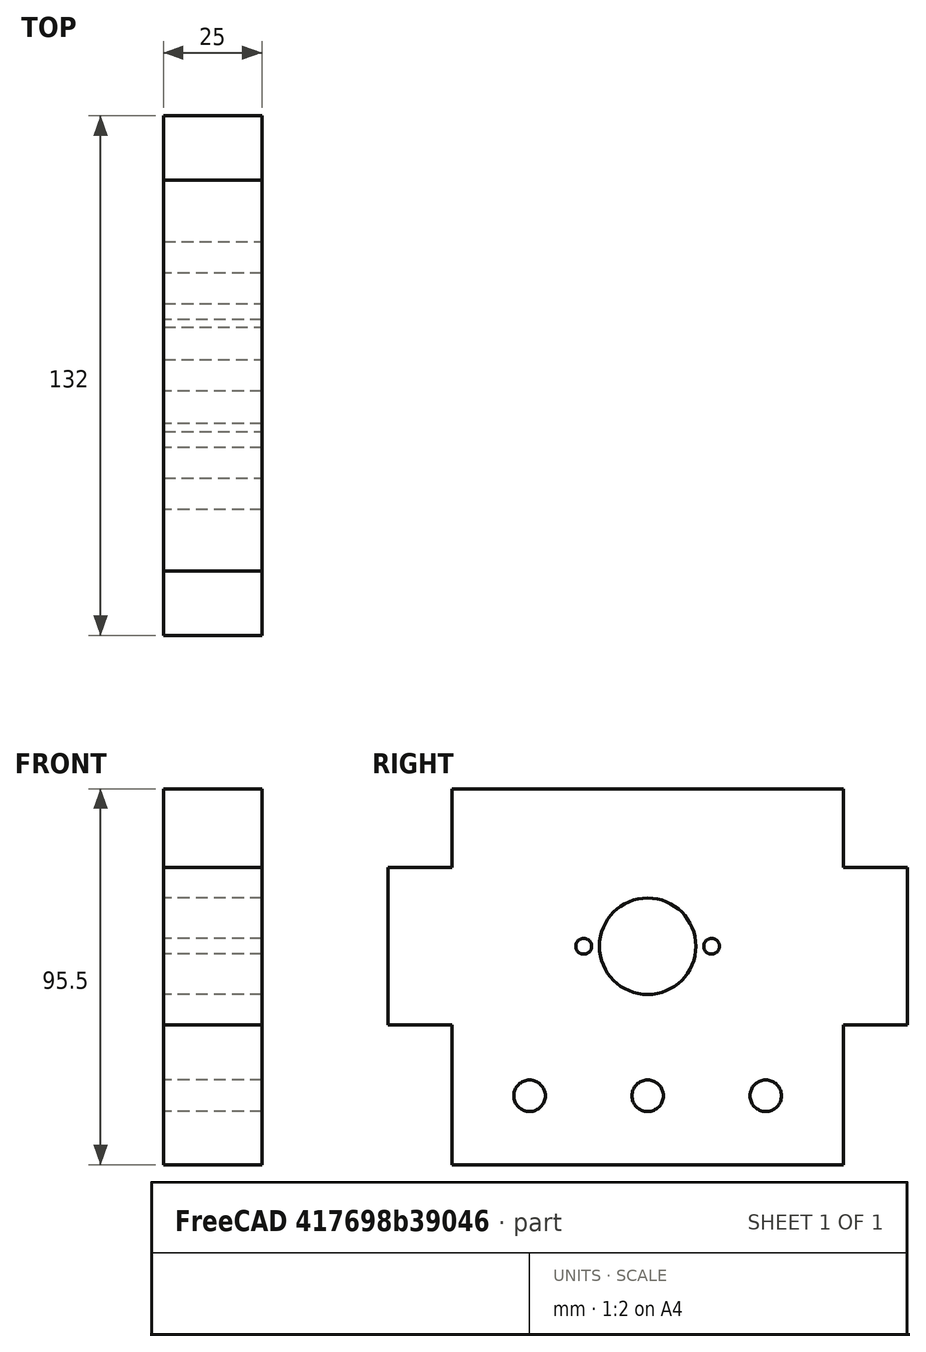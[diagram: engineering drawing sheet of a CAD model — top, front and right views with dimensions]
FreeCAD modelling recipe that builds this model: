
FCSTD DOCUMENT  (FreeCAD 0.19R24267 +99 (Git))
Label: V2 Tabbed end plate FEA_CLEARED
License: All rights reserved
LicenseURL: http://en.wikipedia.org/wiki/All_rights_reserved
objects: Sketcher::SketchObject×4, PartDesign::Pad×4, Fem::ConstraintForce×2, Fem::FeaturePython×2, PartDesign::Body×1, Fem::FemSolverObjectPython×1, App::MaterialObjectPython×1, Fem::ConstraintFixed×1, Fem::FemMeshObjectPython×1, Fem::FemAnalysis×1
note: 13 computed .brp shape members not serialized (recipe doc carries the construction recipe); baked Part::Feature solids carry a one-line shape summary decoded from their .brp

FEATURE [Sketcher::SketchObject] Sketch
  FullyConstrained = true
  MapMode = 5
  Placement = pos=(0,0,0) rot=(0.57735,0.57735,0.57735;2.0944rad)
  Support = -> [YZ_Plane]
  sketch-geometry (41):
    g0: LineSegment StartX=-49.7 StartY=40 StartZ=0 EndX=49.7 EndY=40 EndZ=0
    g1: LineSegment StartX=49.7 StartY=40 StartZ=0 EndX=49.7 EndY=20 EndZ=0
    g2: LineSegment StartX=49.7 StartY=-55.5 StartZ=0 EndX=-49.7 EndY=-55.5 EndZ=0
    g3: LineSegment StartX=-49.7 StartY=-55.5 StartZ=0 EndX=-49.7 EndY=-20 EndZ=0
    g4: Circle CenterX=0 CenterY=0 CenterZ=0 NormalX=0 NormalY=0 NormalZ=1 AngleXU=0 Radius=12.25
    g5: LineSegment StartX=-49.7 StartY=20 StartZ=0 EndX=-66 EndY=20 EndZ=0
    g6: LineSegment StartX=-66 StartY=20 StartZ=0 EndX=-66 EndY=-20 EndZ=0
    g7: LineSegment StartX=-66 StartY=-20 StartZ=0 EndX=-49.7 EndY=-20 EndZ=0
    g8: LineSegment StartX=49.7 StartY=20 StartZ=0 EndX=66 EndY=20 EndZ=0
    g9: LineSegment StartX=49.7 StartY=-20 StartZ=0 EndX=66 EndY=-20 EndZ=0
    g10: LineSegment StartX=66 StartY=20 StartZ=0 EndX=66 EndY=-20 EndZ=0
    g11: LineSegment StartX=-49.7 StartY=20 StartZ=0 EndX=-49.7 EndY=40 EndZ=0
    g12: LineSegment StartX=49.7 StartY=-20 StartZ=0 EndX=49.7 EndY=-55.5 EndZ=0
    g13: Circle CenterX=-16.25 CenterY=0 CenterZ=0 NormalX=0 NormalY=0 NormalZ=1 AngleXU=0 Radius=2
    g14: Circle CenterX=16.25 CenterY=0 CenterZ=0 NormalX=0 NormalY=0 NormalZ=1 AngleXU=0 Radius=2
    g15: Circle CenterX=0 CenterY=0 CenterZ=0 NormalX=0 NormalY=0 NormalZ=1 AngleXU=0 Radius=20.25
    g16: Circle CenterX=-16.25 CenterY=0 CenterZ=0 NormalX=0 NormalY=0 NormalZ=1 AngleXU=0 Radius=4
    g17: Circle CenterX=16.25 CenterY=0 CenterZ=0 NormalX=0 NormalY=0 NormalZ=1 AngleXU=0 Radius=4
    g18: LineSegment StartX=-16.25 StartY=2 StartZ=0 EndX=-16.25 EndY=-2 EndZ=0
    g19: LineSegment StartX=-18.25 StartY=0 StartZ=0 EndX=-14.25 EndY=0 EndZ=0
    g20: LineSegment StartX=14.25 StartY=0 StartZ=0 EndX=18.25 EndY=0 EndZ=0
    g21: LineSegment StartX=16.25 StartY=2 StartZ=0 EndX=16.25 EndY=-2 EndZ=0
    g22: Circle CenterX=0 CenterY=-38 CenterZ=0 NormalX=0 NormalY=0 NormalZ=1 AngleXU=0 Radius=4
    g23: LineSegment StartX=-30 StartY=-38 StartZ=0 EndX=30 EndY=-38 EndZ=0
    g24: Circle CenterX=-30 CenterY=-38 CenterZ=0 NormalX=0 NormalY=0 NormalZ=1 AngleXU=0 Radius=4
    g25: Circle CenterX=30 CenterY=-38 CenterZ=0 NormalX=0 NormalY=0 NormalZ=1 AngleXU=0 Radius=4
    g26: GeomPoint X=0 Y=-55.5 Z=0
    g27: Circle CenterX=0 CenterY=0 CenterZ=0 NormalX=0 NormalY=0 NormalZ=1 AngleXU=0 Radius=13.4
    g28: Circle CenterX=0 CenterY=-42.25 CenterZ=0 NormalX=0 NormalY=0 NormalZ=1 AngleXU=0 Radius=8.25
    g29: GeomPoint X=0 Y=-34 Z=0
    g30: GeomPoint X=0 Y=-42 Z=0
    g31: GeomPoint X=0 Y=-50.5 Z=0
    g32: GeomPoint X=0 Y=35.75 Z=0
    g33: GeomPoint X=0 Y=31.5 Z=0
    g34: GeomPoint X=0 Y=40 Z=0
    g35: LineSegment StartX=-30 StartY=-34 StartZ=0 EndX=-30 EndY=-42 EndZ=0
    g36: LineSegment StartX=-34 StartY=-38 StartZ=0 EndX=-26 EndY=-38 EndZ=0
    g37: LineSegment StartX=-4 StartY=-38 StartZ=0 EndX=4 EndY=-38 EndZ=0
    g38: LineSegment StartX=0 StartY=-42 StartZ=0 EndX=0 EndY=-34 EndZ=0
    g39: LineSegment StartX=30 StartY=-34 StartZ=0 EndX=30 EndY=-42 EndZ=0
    g40: LineSegment StartX=26 StartY=-38 StartZ=0 EndX=34 EndY=-38 EndZ=0
  constraints (116):
    c: Coincident(g0,g1)
    c: Coincident(g12,g2)
    c: Coincident(g2,g3)
    c: Coincident(g11,g0)
    c: Horizontal(g2)
    c: Vertical(g3)
    c: Coincident(g4,g-1)
    c: DistanceX(g0,g0) = 99.4
    c: Symmetric(g0,g0,g-2)
    c: DistanceY(g4,g0) = 40
    c: Horizontal(g5)
    c: Coincident(g6,g5)
    c: Coincident(g7,g6)
    c: Horizontal(g7)
    c: Symmetric(g5,g6,g-1)
    c: Horizontal(g8)
    c: Coincident(g10,g8)
    c: Coincident(g10,g9)
    c: Symmetric(g5,g8,g-2)
    c: Symmetric(g6,g9,g-2)
    c: Horizontal(g9)
    c: DistanceY(g6,g6) = 40
    c: Coincident(g3,g7)
    c: Coincident(g11,g5)
    c: Tangent(g3,g11)
    c: Coincident(g1,g8)
    c: Coincident(g12,g9)
    c: Tangent(g1,g12)
    c: DistanceX(g6,g9) = 132
    c: PointOnObject(g13,g-1)
    c: Symmetric(g14,g13,g-2)
    c: Equal(g13,g14)
    c: Coincident(g15,g4)
    c: Coincident(g16,g13)
    c: Coincident(g17,g14)
    c: DistanceX(g13,g14) = 32.5
    c: Equal(g17,g16)
    c: Diameter(g4) = 24.5
    c: Diameter(g15) = 40.5
    c: Diameter(g13) = 4
    c: PointOnObject(g18,g13)
    c: PointOnObject(g18,g13)
    c: PointOnObject(g19,g13)
    c: PointOnObject(g19,g13)
    c: Horizontal(g19)
    c: PointOnObject(g20,g14)
    c: PointOnObject(g20,g14)
    c: Horizontal(g20)
    c: PointOnObject(g21,g14)
    c: PointOnObject(g21,g14)
    c: Vertical(g21)
    c: PointOnObject(g14,g21)
    c: PointOnObject(g14,g20)
    c: Vertical(g18)
    c: PointOnObject(g13,g18)
    c: PointOnObject(g13,g19)
    c: Diameter(g16) = 8
    c: Vertical(g12)
    c: PointOnObject(g22,g-2)
    c: PointOnObject(g22,g23)
    c: Coincident(g24,g23)
    c: Coincident(g25,g23)
    c: Equal(g24,g22)
    c: Equal(g22,g25)
    c: Diameter(g24) = 8
    c: Symmetric(g24,g25,g-2)
    c: DistanceX(g23,g23) = 60
    c: PointOnObject(g26,g2)
    c: PointOnObject(g26,g-2)
    c: Coincident(g27,g4)
    c: Diameter(g27) = 26.8
    c: DistanceY(g22,g4) = 38
    c: PointOnObject(g28,g-2)
    c: PointOnObject(g29,g-2)
    c: PointOnObject(g29,g22)
    c: PointOnObject(g29,g28)
    c: PointOnObject(g30,g22)
    c: PointOnObject(g31,g28)
    c: PointOnObject(g31,g-2)
    c: PointOnObject(g30,g-2)
    c: DistanceY(g31,g30) = 8.5
    c: DistanceY(g26,g31) = 5
    c: DistanceY(g26,g28) = 13.25
    c: PointOnObject(g32,g-2)
    c: DistanceY(g4,g32) = 35.75
    c: DistanceY(g26,g22) = 17.5
    c: PointOnObject(g33,g-2)
    c: PointOnObject(g34,g0)
    c: Symmetric(g34,g33,g32)
    c: DistanceY(g33,g34) = 8.5
    c: PointOnObject(g35,g24)
    c: PointOnObject(g35,g24)
    c: Vertical(g35)
    c: PointOnObject(g36,g24)
    c: PointOnObject(g36,g24)
    c: Horizontal(g36)
    c: PointOnObject(g37,g22)
    c: PointOnObject(g37,g22)
    c: PointOnObject(g38,g22)
    c: PointOnObject(g38,g22)
    c: PointOnObject(g39,g25)
    c: PointOnObject(g39,g25)
    c: Vertical(g39)
    c: PointOnObject(g40,g25)
    c: PointOnObject(g40,g25)
    c: Horizontal(g40)
    c: PointOnObject(g24,g35)
    c: PointOnObject(g24,g36)
    c: PointOnObject(g22,g38)
    c: PointOnObject(g22,g37)
    c: PointOnObject(g25,g39)
    c: PointOnObject(g25,g40)
    c: Horizontal(g37)
    c: Vertical(g38)
    c: Diameter(g28) = 16.5
    c: DistanceY(g2,g4) = 55.5
FEATURE [PartDesign::Pad] Pad
  Direction = (1,1,1)
  Length = 25
  Length2 = 100
  Midplane = true
  Placement = pos=(0,0,0) rot=(0.57735,0.57735,0.57735;2.0944rad)
  Profile = -> Sketch
  Type = 0
FEATURE [Sketcher::SketchObject] Sketch001  label="Load point left"
  FullyConstrained = true
  MapMode = 5
  Placement = pos=(0,0,0) rot=(0.57735,0.57735,0.57735;2.0944rad)
  Support = -> [YZ_Plane]
  sketch-geometry (4):
    g0: LineSegment StartX=-58 StartY=20 StartZ=0 EndX=-50 EndY=20 EndZ=0
    g1: LineSegment StartX=-50 StartY=20 StartZ=0 EndX=-50 EndY=-20 EndZ=0
    g2: LineSegment StartX=-50 StartY=-20 StartZ=0 EndX=-58 EndY=-20 EndZ=0
    g3: LineSegment StartX=-58 StartY=-20 StartZ=0 EndX=-58 EndY=20 EndZ=0
  constraints (11):
    c: Coincident(g0,g1)
    c: Coincident(g1,g2)
    c: Coincident(g2,g3)
    c: Coincident(g3,g0)
    c: Horizontal(g0)
    c: Horizontal(g2)
    c: Vertical(g3)
    c: DistanceY(g2,g0) = 40
    c: Symmetric(g0,g1,g-1)
    c: DistanceX(g0,g0) = 8
    c: DistanceX(g0,g-1) = 50
FEATURE [PartDesign::Pad] Pad001  label="Load point left pad"
  BaseFeature = -> Pad
  Direction = (1,1,1)
  Length = 25
  Length2 = 100
  Midplane = true
  Placement = pos=(0,0,0) rot=(0.57735,0.57735,0.57735;2.0944rad)
  Profile = -> Sketch001
  Type = 0
FEATURE [Sketcher::SketchObject] Sketch002  label="Load point right"
  FullyConstrained = true
  MapMode = 5
  Placement = pos=(0,0,0) rot=(0.57735,0.57735,0.57735;2.0944rad)
  Support = -> [YZ_Plane]
  sketch-geometry (4):
    g0: LineSegment StartX=50 StartY=20 StartZ=0 EndX=58 EndY=20 EndZ=0
    g1: LineSegment StartX=58 StartY=20 StartZ=0 EndX=58 EndY=-20 EndZ=0
    g2: LineSegment StartX=58 StartY=-20 StartZ=0 EndX=50 EndY=-20 EndZ=0
    g3: LineSegment StartX=50 StartY=-20 StartZ=0 EndX=50 EndY=20 EndZ=0
  constraints (11):
    c: Coincident(g0,g1)
    c: Coincident(g1,g2)
    c: Coincident(g2,g3)
    c: Coincident(g3,g0)
    c: Horizontal(g0)
    c: Horizontal(g2)
    c: Vertical(g1)
    c: DistanceX(g-1,g0) = 50
    c: DistanceX(g0,g0) = 8
    c: Symmetric(g0,g2,g-1)
    c: DistanceY(g1,g1) = 40
FEATURE [PartDesign::Pad] Pad002  label="Load point right pad"
  BaseFeature = -> Pad001
  Direction = (1,1,1)
  Length = 25
  Length2 = 100
  Midplane = true
  Placement = pos=(0,0,0) rot=(0.57735,0.57735,0.57735;2.0944rad)
  Profile = -> Sketch002
  Type = 0
FEATURE [Sketcher::SketchObject] Sketch003  label="Load pad center"
  FullyConstrained = true
  MapMode = 5
  Placement = pos=(0,0,0) rot=(0.57735,0.57735,0.57735;2.0944rad)
  Support = -> [YZ_Plane]
  sketch-geometry (4):
    g0: Circle CenterX=0 CenterY=0 CenterZ=0 NormalX=0 NormalY=0 NormalZ=1 AngleXU=0 Radius=20.25
    g1: Circle CenterX=0 CenterY=0 CenterZ=0 NormalX=0 NormalY=0 NormalZ=1 AngleXU=0 Radius=12.25
    g2: Circle CenterX=-16.25 CenterY=0 CenterZ=0 NormalX=0 NormalY=0 NormalZ=1 AngleXU=0 Radius=2
    g3: Circle CenterX=16.25 CenterY=0 CenterZ=0 NormalX=0 NormalY=0 NormalZ=1 AngleXU=0 Radius=2
  constraints (9):
    c: Coincident(g0,g-1)
    c: Coincident(g1,g0)
    c: Diameter(g1) = 24.5
    c: Diameter(g0) = 40.5
    c: PointOnObject(g2,g-1)
    c: Symmetric(g2,g3,g-2)
    c: DistanceX(g2,g3) = 32.5
    c: Equal(g2,g3)
    c: Diameter(g3) = 4
FEATURE [PartDesign::Pad] Pad003  label="Load pad center pad"
  BaseFeature = -> Pad002
  Direction = (1,1,1)
  Length = 25
  Length2 = 100
  Midplane = true
  Placement = pos=(0,0,0) rot=(0.57735,0.57735,0.57735;2.0944rad)
  Profile = -> Sketch003
  Type = 0
FEATURE [PartDesign::Body] Body
  Group = -> [Sketch,Pad,Sketch001,Pad001,Sketch002,Pad002,Sketch003,Pad003]
  Origin = -> Origin
  Tip = -> Pad003
FEATURE [Fem::FemSolverObjectPython] SolverCcxTools  # FEM object (typed FeaturePython)
  AnalysisType = 0
  BeamShellResultOutput3D = false
  EigenmodeHighLimit = 1000000
  EigenmodeLowLimit = 0
  EigenmodesCount = 10
  GeometricalNonlinearity = 0
  IterationsControlParameterCutb = 0.25,0.5,0.75,0.85,,,1.5,
  IterationsControlParameterIter = 4,8,9,200,10,400,,200,,
  IterationsControlParameterTimeUse = false
  IterationsThermoMechMaximum = 2000
  IterationsUserDefinedIncrementations = false
  IterationsUserDefinedTimeStepLength = false
  MaterialNonlinearity = 0
  MatrixSolverType = 0
  SplitInputWriter = false
  ThermoMechSteadyState = true
  TimeEnd = 1
  TimeInitialStep = 0.01
FEATURE [App::MaterialObjectPython] MaterialSolid  # material (typed FeaturePython)
  Category = 0
  Material = AuthorAndLicense=CalculiX-Steel; CardName=CalculiX-Steel; Density=7900 kg/m^3; Description=Standard steel material for CalculiX sample calculations; Father=Metal; Name=CalculiX-Steel; PoissonRatio=0.3; SpecificHeat=590 J/kg/K; ThermalConductivity=43 W/m/K; ThermalExpansionCoefficient=0.000012 m/m/K; YoungsModulus=210000 MPa
FEATURE [Fem::ConstraintForce] ConstraintForce
  DirectionVector = (-1,4e-16,-1.4e-15)
  Force = 30000
  NormalDirection = (1,-4e-16,1.4e-15)
  Reversed = true
FEATURE [Fem::ConstraintForce] ConstraintForce001
  DirectionVector = (1,-2e-16,1.9e-15)
  Force = 30000
  NormalDirection = (-1,2e-16,-1.9e-15)
  Reversed = true
FEATURE [Fem::ConstraintFixed] ConstraintFixed
  NormalDirection = (0,0,1)
FEATURE [Fem::FeaturePython] MeshRegion  # FEM object (typed FeaturePython)
  CharacteristicLength = 1.4
FEATURE [Fem::FeaturePython] MeshRegion001  # FEM object (typed FeaturePython)
  CharacteristicLength = 0.28
FEATURE [Fem::FemMeshObjectPython] FEMMeshGmsh  # FEM object (typed FeaturePython)
  Algorithm2D = 0
  Algorithm3D = 0
  CharacteristicLengthMax = 8
  CharacteristicLengthMin = 0
  CoherenceMesh = true
  ElementDimension = 0
  ElementOrder = 1
  GeometryTolerance = 1e-06
  GroupsOfNodes = false
  HighOrderOptimize = false
  MeshRegionList = -> [MeshRegion,MeshRegion001]
  OptimizeNetgen = false
  OptimizeStd = true
  RecombineAll = false
  SecondOrderLinear = false
FEATURE [Fem::FemAnalysis] Analysis
  Group = -> [SolverCcxTools,MaterialSolid,ConstraintForce,ConstraintForce001,ConstraintFixed,FEMMeshGmsh]
